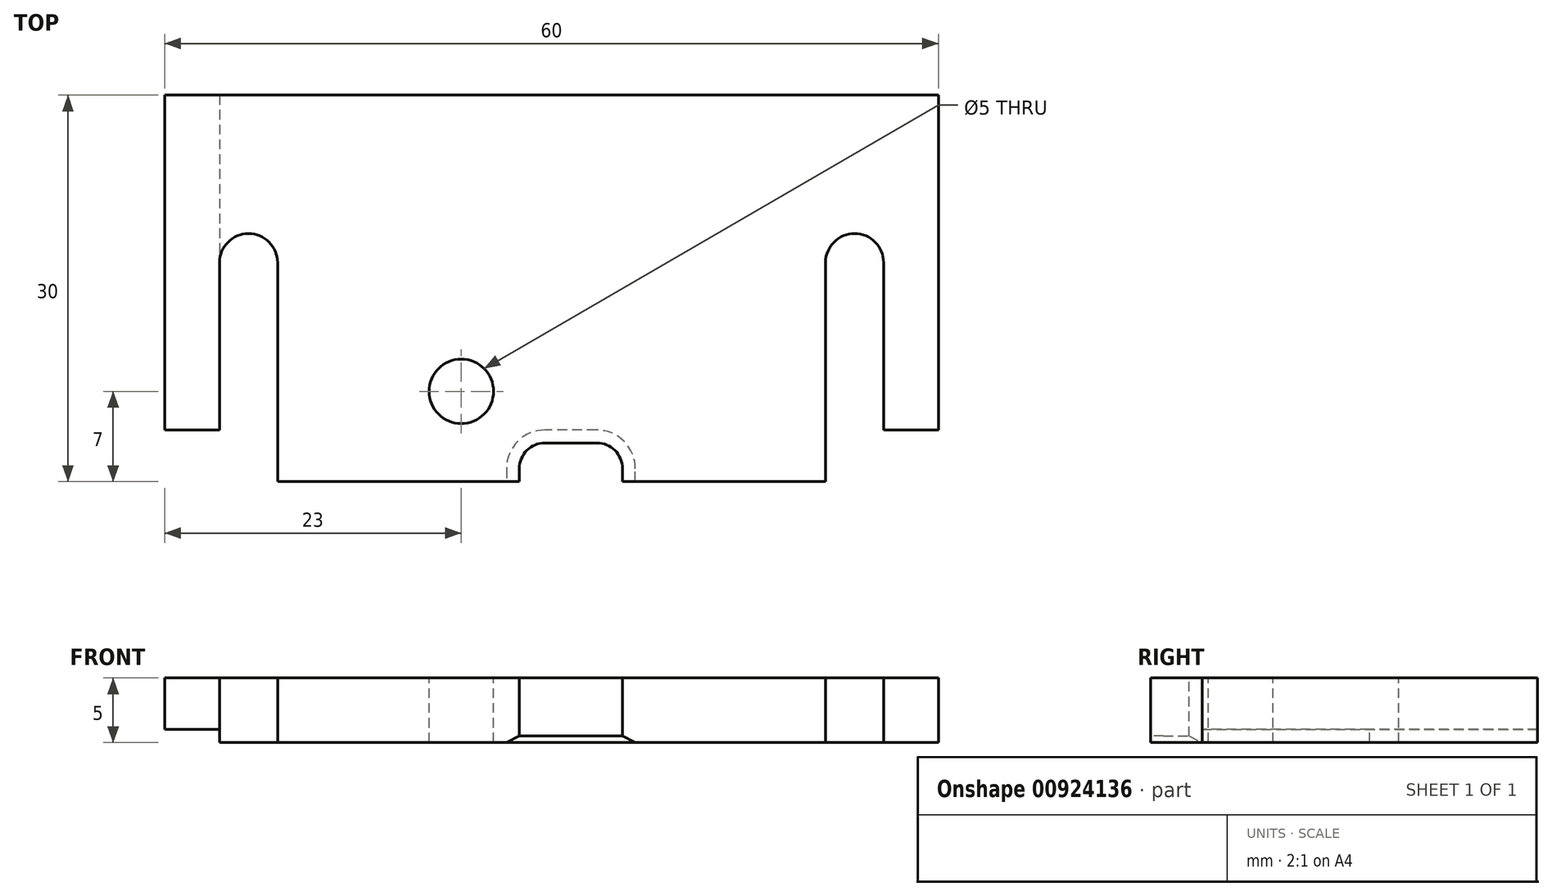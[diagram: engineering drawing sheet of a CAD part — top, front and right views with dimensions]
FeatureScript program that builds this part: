
annotation { "Feature Type Name" : "Feature", "Feature Type Description" : "" }
export const myFeature = defineFeature(function(context is Context, id is Id, definition is map)
    precondition{}
    {
        {
            var Q0;
            Q0=qCreatedBy(makeId("Top.planeOp"),FACE);
            var sketch = newSketch(context, id + "F0", { "sketchPlane" : qUnion([Q0])});
            skLineSegment(sketch, "E0", {"start": v(0, 0) * mm, "end": v(60, 0) * mm});
            skLineSegment(sketch, "E1", {"start": v(60, 0) * mm, "end": v(60, -26) * mm});
            skLineSegment(sketch, "E2", {"start": v(60, -26) * mm, "end": v(55.75, -26) * mm});
            skLineSegment(sketch, "E3", {"start": v(55.75, -26) * mm, "end": v(55.75, -13) * mm});
            skLineSegment(sketch, "E4", {"start": v(55.75, -13) * mm, "end": v(51.25, -13) * mm, "construction": true});
            skLineSegment(sketch, "E5", {"start": v(51.25, -13) * mm, "end": v(51.25, -30) * mm});
            skLineSegment(sketch, "E6", {"start": v(51.25, -30) * mm, "end": v(35.5, -30) * mm});
            skLineSegment(sketch, "E7", {"start": v(35.5, -30) * mm, "end": v(35.5, -29) * mm});
            skLineSegment(sketch, "E8", {"start": v(33.5, -27) * mm, "end": v(29.5, -27) * mm});
            skLineSegment(sketch, "E9", {"start": v(27.5, -29) * mm, "end": v(27.5, -30) * mm});
            skLineSegment(sketch, "E10", {"start": v(27.5, -30) * mm, "end": v(8.75, -30) * mm});
            skLineSegment(sketch, "E11", {"start": v(8.75, -30) * mm, "end": v(8.75, -13) * mm});
            skLineSegment(sketch, "E12", {"start": v(8.75, -13) * mm, "end": v(4.25, -13) * mm, "construction": true});
            skLineSegment(sketch, "E13", {"start": v(4.25, -13) * mm, "end": v(4.25, -26) * mm});
            skLineSegment(sketch, "E14", {"start": v(4.25, -26) * mm, "end": v(0, -26) * mm});
            skLineSegment(sketch, "E15", {"start": v(0, -26) * mm, "end": v(0, 0) * mm});
            skPoint(sketch, "E16.visualSharp", {"position": v(27.5, -27) * mm});
            skArc(sketch, "E16.filletArc", {"start": v(29.5, -27) * mm, "mid": v(28.09, -27.59) * mm, "end": v(27.5, -29) * mm});
            skPoint(sketch, "E17.visualSharp", {"position": v(35.5, -27) * mm});
            skArc(sketch, "E17.filletArc", {"start": v(35.5, -29) * mm, "mid": v(34.91, -27.59) * mm, "end": v(33.5, -27) * mm});
            skArc(sketch, "E18", {"start": v(8.75, -13) * mm, "mid": v(6.5, -10.75) * mm, "end": v(4.25, -13) * mm});
            skArc(sketch, "E19", {"start": v(55.75, -13) * mm, "mid": v(53.5, -10.75) * mm, "end": v(51.25, -13) * mm});
            skPoint(sketch, "E20", {"position": v(23, -23) * mm});
            skSolve(sketch);
        }
        {
            var Q0;
            Q0 = qSketchRegion(id + "F0", true);
            extrude(context, id + "F1", {"entities" : qUnion([Q0]), "oppositeDirection" : true, "depth" : 5 * mm, "offsetDistance" : 25 * mm});
        }
        {
            var Q0;
            Q0=sQuery(id+"F0.wireOp",VERTEX,"E20");
            var Q1;
            Q1=makeQuery(id+"F1.opExtrude","SWEPT_BODY",BODY,{"disambiguationData":[OSD([sQuery(id+"F0.wireOp",EDGE,"E0"),sQuery(id+"F0.wireOp",EDGE,"E1"),sQuery(id+"F0.wireOp",EDGE,"E2"),sQuery(id+"F0.wireOp",EDGE,"E3"),sQuery(id+"F0.wireOp",EDGE,"E5"),sQuery(id+"F0.wireOp",EDGE,"E6"),sQuery(id+"F0.wireOp",EDGE,"E7"),sQuery(id+"F0.wireOp",EDGE,"E8"),sQuery(id+"F0.wireOp",EDGE,"E9"),sQuery(id+"F0.wireOp",EDGE,"E10"),sQuery(id+"F0.wireOp",EDGE,"E11"),sQuery(id+"F0.wireOp",EDGE,"E13"),sQuery(id+"F0.wireOp",EDGE,"E14"),sQuery(id+"F0.wireOp",EDGE,"E15"),sQuery(id+"F0.wireOp",EDGE,"E16.filletArc"),sQuery(id+"F0.wireOp",EDGE,"E17.filletArc"),sQuery(id+"F0.wireOp",EDGE,"E18"),sQuery(id+"F0.wireOp",EDGE,"E19")])]});
            hole(context, id + "F2", {"style" : HoleStyle.SIMPLE, "endStyle" : HoleEndStyle.THROUGH, "standardTappedOrClearance" : lookupTablePath({ "standard" : "ISO", "size" : "5", "type" : "Drilled" }), "standardBlindInLast" : lookupTablePath({ "standard" : "ISO", "size" : "5", "type" : "Drilled" }), "holeDiameter" : 5 * mm, "majorDiameter" : 5 * mm, "isTappedThrough" : true, "tappedDepth" : 18.6 * mm, "tapClearance" : 3, "startFromSketch" : true, "locations" : qUnion([Q0]), "scope" : qUnion([Q1])});
        }
        {
            var Q0;
            Q0=makeQuery(id+"F1.opExtrude","CAP_EDGE",EDGE,{"disambiguationData":[OSD([sQuery(id+"F0.wireOp",EDGE,"E8")])],"isStart":false});
            chamfer(context, id + "F3", {"entities" : qUnion([Q0]), "chamferType" : ChamferType.TWO_OFFSETS, "width1" : 1 * mm, "oppositeDirection" : false, "width2" : 0.5 * mm, "tangentPropagation" : true});
        }
        {
            var Q0;
            Q0=makeQuery(id+"F1.opExtrude","CAP_FACE",FACE,{"disambiguationData":[OSD([sQuery(id+"F0.wireOp",EDGE,"E0"),sQuery(id+"F0.wireOp",EDGE,"E1"),sQuery(id+"F0.wireOp",EDGE,"E2"),sQuery(id+"F0.wireOp",EDGE,"E3"),sQuery(id+"F0.wireOp",EDGE,"E5"),sQuery(id+"F0.wireOp",EDGE,"E6"),sQuery(id+"F0.wireOp",EDGE,"E7"),sQuery(id+"F0.wireOp",EDGE,"E8"),sQuery(id+"F0.wireOp",EDGE,"E9"),sQuery(id+"F0.wireOp",EDGE,"E10"),sQuery(id+"F0.wireOp",EDGE,"E11"),sQuery(id+"F0.wireOp",EDGE,"E13"),sQuery(id+"F0.wireOp",EDGE,"E14"),sQuery(id+"F0.wireOp",EDGE,"E15"),sQuery(id+"F0.wireOp",EDGE,"E16.filletArc"),sQuery(id+"F0.wireOp",EDGE,"E17.filletArc"),sQuery(id+"F0.wireOp",EDGE,"E18"),sQuery(id+"F0.wireOp",EDGE,"E19")])],"isStart":false});
            var sketch = newSketch(context, id + "F4", { "sketchPlane" : qUnion([Q0])});
            skLineSegment(sketch, "E21.bottom", {"start": v(0, 0) * mm, "end": v(4.25, 0) * mm});
            skLineSegment(sketch, "E21.top", {"start": v(0, 26) * mm, "end": v(4.25, 26) * mm});
            skLineSegment(sketch, "E21.left", {"start": v(0, 0) * mm, "end": v(0, 26) * mm});
            skLineSegment(sketch, "E21.right", {"start": v(4.25, 0) * mm, "end": v(4.25, 26) * mm});
            skSolve(sketch);
        }
        {
            var Q0;
            Q0 = qSketchRegion(id + "F4", true);
            extrude(context, id + "F5", {"entities" : qUnion([Q0]), "operationType" : NewBodyOperationType.REMOVE, "oppositeDirection" : true, "depth" : 1 * mm, "offsetDistance" : 25 * mm});
        }
    });
